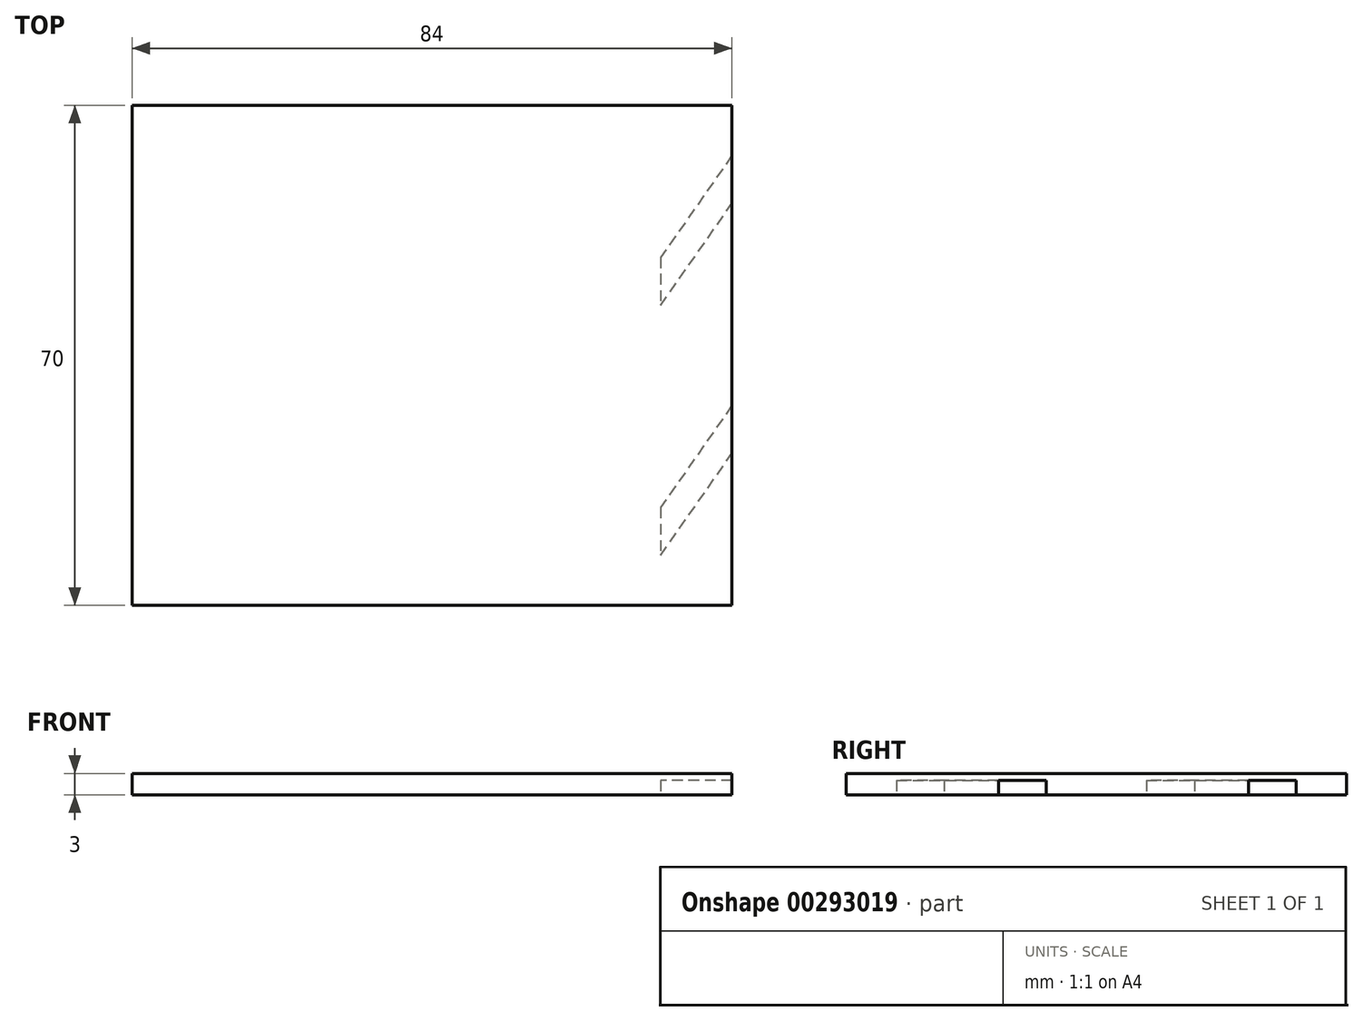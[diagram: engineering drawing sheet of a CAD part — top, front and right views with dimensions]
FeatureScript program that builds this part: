
annotation { "Feature Type Name" : "Feature", "Feature Type Description" : "" }
export const myFeature = defineFeature(function(context is Context, id is Id, definition is map)
    precondition{}
    {
        {
            var Q0;
            Q0=qCreatedBy(makeId("Front.planeOp"),FACE);
            var sketch = newSketch(context, id + "F0", { "sketchPlane" : qUnion([Q0])});
            skLineSegment(sketch, "E0.bottom", {"start": v(0, -23) * mm, "end": v(42, -23) * mm});
            skLineSegment(sketch, "E0.top", {"start": v(0, -20) * mm, "end": v(42, -20) * mm});
            skLineSegment(sketch, "E0.left", {"start": v(0, -23) * mm, "end": v(0, -20) * mm});
            skLineSegment(sketch, "E0.right", {"start": v(42, -23) * mm, "end": v(42, -20) * mm});
            skLineSegment(sketch, "E1", {"start": v(0, 0) * mm, "end": v(0, -20) * mm, "construction": true});
            skLineSegment(sketch, "E2", {"start": v(42, -21.5) * mm, "end": v(34, -21.5) * mm, "construction": true});
            skPoint(sketch, "E2.endSnap0", {"position": v(42, -21.5) * mm});
            skLineSegment(sketch, "E3", {"start": v(34, -21.5) * mm, "end": v(32, -21.5) * mm, "construction": true});
            skLineSegment(sketch, "E4", {"start": v(32, -21.5) * mm, "end": v(30, -21.5) * mm, "construction": true});
            skLineSegment(sketch, "E5", {"start": v(30, -21.5) * mm, "end": v(21, -21.5) * mm, "construction": true});
            skLineSegment(sketch, "E6", {"start": v(21, -21.5) * mm, "end": v(17, -21.5) * mm, "construction": true});
            skLineSegment(sketch, "E7", {"start": v(17, -21.5) * mm, "end": v(0, -21.5) * mm, "construction": true});
            skLineSegment(sketch, "E8", {"start": v(32, -21.5) * mm, "end": v(32, -23) * mm, "construction": true});
            skLineSegment(sketch, "E9", {"start": v(32, -23) * mm, "end": v(32, -21) * mm});
            skPoint(sketch, "E9.endSnap0", {"position": v(32, -22.25) * mm});
            skLineSegment(sketch, "E10", {"start": v(32, -21) * mm, "end": v(42, -21) * mm});
            skLineSegment(sketch, "E11", {"start": v(32, -22.25) * mm, "end": v(38, -22.25) * mm, "construction": true});
            skLineSegment(sketch, "E12", {"start": v(38, -22.25) * mm, "end": v(38, -23) * mm});
            skLineSegment(sketch, "E13", {"start": v(38, -23) * mm, "end": v(38, -21) * mm});
            skLineSegment(sketch, "E14.MirrorCS", {"start": v(-32, -23) * mm, "end": v(-32, -21) * mm});
            skLineSegment(sketch, "E15.MirrorCS", {"start": v(-32, -21.5) * mm, "end": v(-32, -23) * mm, "construction": true});
            skLineSegment(sketch, "E16.MirrorCS", {"start": v(-34, -21.5) * mm, "end": v(-32, -21.5) * mm, "construction": true});
            skLineSegment(sketch, "E17.MirrorCS", {"start": v(-32, -21.5) * mm, "end": v(-30, -21.5) * mm, "construction": true});
            skLineSegment(sketch, "E18.MirrorCS", {"start": v(-38, -23) * mm, "end": v(-38, -21) * mm});
            skLineSegment(sketch, "E19.MirrorCS", {"start": v(-38, -22.25) * mm, "end": v(-38, -23) * mm});
            skLineSegment(sketch, "E20.MirrorCS", {"start": v(-42, -23) * mm, "end": v(-42, -20) * mm});
            skLineSegment(sketch, "E21.MirrorCS", {"start": v(-42, -21.5) * mm, "end": v(-34, -21.5) * mm, "construction": true});
            skLineSegment(sketch, "E22.MirrorCS", {"start": v(-32, -21) * mm, "end": v(-42, -21) * mm});
            skLineSegment(sketch, "E23.MirrorCS", {"start": v(-32, -22.25) * mm, "end": v(-38, -22.25) * mm, "construction": true});
            skPoint(sketch, "E24.MirrorP", {"position": v(-42, -21.5) * mm});
            skLineSegment(sketch, "E25.MirrorCS", {"start": v(-30, -21.5) * mm, "end": v(-21, -21.5) * mm, "construction": true});
            skPoint(sketch, "E26.MirrorP", {"position": v(-32, -22.25) * mm});
            skLineSegment(sketch, "E27.MirrorCS", {"start": v(-21, -21.5) * mm, "end": v(-17, -21.5) * mm, "construction": true});
            skLineSegment(sketch, "E28.MirrorCS", {"start": v(-21, 40) * mm, "end": v(-17, 40) * mm});
            skLineSegment(sketch, "E29.MirrorCS", {"start": v(-30, 40) * mm, "end": v(-34, 40) * mm});
            skLineSegment(sketch, "E30.MirrorCS", {"start": v(0, -23) * mm, "end": v(-42, -23) * mm});
            skLineSegment(sketch, "E31.MirrorCS", {"start": v(-30, 40) * mm, "end": v(-30, -21.5) * mm});
            skLineSegment(sketch, "E32.MirrorCS", {"start": v(-17, 40) * mm, "end": v(-17, -21.5) * mm});
            skLineSegment(sketch, "E33.MirrorCS", {"start": v(-34, -21.5) * mm, "end": v(-34, 40) * mm});
            skLineSegment(sketch, "E34.MirrorCS", {"start": v(0, -20) * mm, "end": v(-42, -20) * mm});
            skLineSegment(sketch, "E35.MirrorCS", {"start": v(-17, -21.5) * mm, "end": v(0, -21.5) * mm, "construction": true});
            skLineSegment(sketch, "E36.MirrorCS", {"start": v(-21, -21.5) * mm, "end": v(-21, 40) * mm});
            skSolve(sketch);
        }
        {
            var Q0;
            {var subQ5=sQuery(id+"F0.wireOp",EDGE,"rBg3Q4IR-CGkZ-PO5m-HV7D-72pnYfLjL1so");Q0=makeQuery(id+"F0.imprint","IMPRINT",FACE,{"disambiguationData":[TD([[makeQuery(id+"F0.imprint","IMPRINT",EDGE,{"derivedFrom":subQ5}),1.0]])]});}
            var Q1;
            {var subQ5=sQuery(id+"F0.wireOp",EDGE,"dkqnGSy7-Vz6o-ykO8-f6sr-zODuD2kIRj3Q");Q1=makeQuery(id+"F0.imprint","IMPRINT",FACE,{"disambiguationData":[TD([[makeQuery(id+"F0.imprint","IMPRINT",EDGE,{"derivedFrom":subQ5}),-1.0]])]});}
            var Q2;
            {var subQ10=sQuery(id+"F0.wireOp",EDGE,"E9");Q2=makeQuery(id+"F0.imprint","IMPRINT",FACE,{"disambiguationData":[TD([[makeQuery(id+"F0.imprint","IMPRINT",EDGE,{"derivedFrom":subQ10}),1.0]])]});}
            var Q3;
            {var subQ1=sQuery(id+"F0.wireOp",EDGE,"E0.right");var subQ4=sQuery(id+"F0.wireOp",EDGE,"E0.top");var subQ5=makeQuery(id+"F0.imprint","INTERSECT",VERTEX,{"derivedFrom":[subQ4,subQ1]});Q3=makeQuery(id+"F0.imprint","IMPRINT",FACE,{"disambiguationData":[TD([[makeQuery(id+"F0.imprint","IMPRINT",EDGE,{"disambiguationData":[TD([[subQ5,1.0]])],"derivedFrom":subQ4}),-1.0]])]});}
            var Q4;
            {var subQ4=sQuery(id+"F0.wireOp",EDGE,"E9");Q4=makeQuery(id+"F0.imprint","IMPRINT",FACE,{"disambiguationData":[TD([[makeQuery(id+"F0.imprint","IMPRINT",EDGE,{"derivedFrom":subQ4}),-1.0]])]});}
            var Q5;
            {var subQ0=sQuery(id+"F0.wireOp",EDGE,"E13");var subQ3=makeQuery(id+"F0.imprint","IMPRINT",VERTEX,{"derivedFrom":subQ0});Q5=makeQuery(id+"F0.imprint","IMPRINT",FACE,{"disambiguationData":[TD([[makeQuery(id+"F0.imprint","IMPRINT",EDGE,{"disambiguationData":[TD([[subQ3,1.0]])],"derivedFrom":subQ0}),-1.0]])]});}
            var Q6;
            {var subQ6=sQuery(id+"F0.wireOp",EDGE,"E0.left");Q6=makeQuery(id+"F0.imprint","IMPRINT",FACE,{"disambiguationData":[TD([[makeQuery(id+"F0.imprint","IMPRINT",EDGE,{"derivedFrom":subQ6}),1.0]])]});}
            var Q7;
            {var subQ1=sQuery(id+"F0.wireOp",EDGE,"E22.MirrorCS");var subQ8=makeQuery(id+"F0.imprint","INTERSECT",VERTEX,{"derivedFrom":[sQuery(id+"F0.wireOp",EDGE,"E18.MirrorCS"),subQ1]});Q7=makeQuery(id+"F0.imprint","IMPRINT",FACE,{"disambiguationData":[TD([[makeQuery(id+"F0.imprint","IMPRINT",EDGE,{"disambiguationData":[TD([[subQ8,1.0]])],"derivedFrom":subQ1}),-1.0]])]});}
            var Q8;
            {var subQ1=sQuery(id+"F0.wireOp",EDGE,"E18.MirrorCS");var subQ5=makeQuery(id+"F0.imprint","IMPRINT",VERTEX,{"derivedFrom":subQ1});Q8=makeQuery(id+"F0.imprint","IMPRINT",FACE,{"disambiguationData":[TD([[makeQuery(id+"F0.imprint","IMPRINT",EDGE,{"disambiguationData":[TD([[subQ5,1.0]])],"derivedFrom":subQ1}),1.0]])]});}
            var Q9;
            {var subQ1=sQuery(id+"F0.wireOp",EDGE,"E14.MirrorCS");Q9=makeQuery(id+"F0.imprint","IMPRINT",FACE,{"disambiguationData":[TD([[makeQuery(id+"F0.imprint","IMPRINT",EDGE,{"derivedFrom":subQ1}),1.0]])]});}
            extrude(context, id + "F1", {"entities" : qUnion([Q0, Q1, Q2, Q3, Q4, Q5, Q6, Q7, Q8, Q9]), "depth" : 70 * mm});
        }
        {
            var Q0;
            Q0=makeQuery(id+"F1.opExtrude","SWEPT_FACE",FACE,{"disambiguationData":[OSD([sQuery(id+"F0.wireOp",EDGE,"E0.bottom"),sQuery(id+"F0.wireOp",EDGE,"E30.MirrorCS")])]});
            var sketch = newSketch(context, id + "F2", { "sketchPlane" : qUnion([Q0])});
            skLineSegment(sketch, "E37", {"start": v(42, 0) * mm, "end": v(-42, 0) * mm, "construction": true});
            skLineSegment(sketch, "E38", {"start": v(-42, 0) * mm, "end": v(-42, 70) * mm, "construction": true});
            skLineSegment(sketch, "E39", {"start": v(-42, 70) * mm, "end": v(42, 70) * mm, "construction": true});
            skLineSegment(sketch, "E40", {"start": v(0, 70) * mm, "end": v(0, 0) * mm});
            skLineSegment(sketch, "E41", {"start": v(42, 35) * mm, "end": v(42, 0) * mm, "construction": true});
            skLineSegment(sketch, "E42.MirrorCS", {"start": v(-42, 35) * mm, "end": v(42, 35) * mm});
            skLineSegment(sketch, "E43.MirrorCS", {"start": v(42, 35) * mm, "end": v(42, 70) * mm, "construction": true});
            skLineSegment(sketch, "E44", {"start": v(42, 70) * mm, "end": v(42, 0) * mm, "construction": true});
            skLineSegment(sketch, "E45", {"start": v(42, 70) * mm, "end": v(32, 70) * mm, "construction": true});
            skLineSegment(sketch, "E46", {"start": v(32, 70) * mm, "end": v(32, 35) * mm, "construction": true});
            skLineSegment(sketch, "E47", {"start": v(32, 35) * mm, "end": v(42, 35) * mm, "construction": true});
            skLineSegment(sketch, "E48", {"start": v(42, 42) * mm, "end": v(32, 56.28) * mm});
            skLineSegment(sketch, "E49", {"start": v(32, 56.28) * mm, "end": v(32, 63) * mm});
            skLineSegment(sketch, "E50", {"start": v(32, 63) * mm, "end": v(42, 48.72) * mm});
            skLineSegment(sketch, "E51", {"start": v(42, 48.72) * mm, "end": v(42, 42) * mm});
            skLineSegment(sketch, "E52.MirrorCS", {"start": v(-32, 63) * mm, "end": v(-42, 48.72) * mm});
            skLineSegment(sketch, "E53.MirrorCS", {"start": v(-42, 42) * mm, "end": v(-32, 56.28) * mm});
            skLineSegment(sketch, "E54.MirrorCS", {"start": v(-32, 70) * mm, "end": v(-32, 35) * mm, "construction": true});
            skLineSegment(sketch, "E55", {"start": v(-32, 63) * mm, "end": v(-32, 56.28) * mm});
            skLineSegment(sketch, "E56", {"start": v(-42, 48.72) * mm, "end": v(-42, 42) * mm});
            skLineSegment(sketch, "E57", {"start": v(-42, 0) * mm, "end": v(-42, 7) * mm, "construction": true});
            skLineSegment(sketch, "E58", {"start": v(42, 0) * mm, "end": v(42, 7) * mm, "construction": true});
            skLineSegment(sketch, "E59.MirrorCS", {"start": v(-32, 0) * mm, "end": v(-32, 35) * mm, "construction": true});
            skLineSegment(sketch, "E60", {"start": v(32, 35) * mm, "end": v(32, 0) * mm, "construction": true});
            skLineSegment(sketch, "E61", {"start": v(32, 35) * mm, "end": v(32, 28) * mm, "construction": true});
            skLineSegment(sketch, "E62", {"start": v(-32, 35) * mm, "end": v(-32, 28) * mm, "construction": true});
            skLineSegment(sketch, "E63", {"start": v(-42, 7) * mm, "end": v(-32, 21.28) * mm});
            skLineSegment(sketch, "E64", {"start": v(42, 7) * mm, "end": v(32, 21.28) * mm});
            skLineSegment(sketch, "E65", {"start": v(-32, 28) * mm, "end": v(-42, 13.72) * mm});
            skLineSegment(sketch, "E66", {"start": v(32, 28) * mm, "end": v(42, 13.72) * mm});
            skLineSegment(sketch, "E67", {"start": v(42, 13.72) * mm, "end": v(42, 7) * mm});
            skLineSegment(sketch, "E68", {"start": v(32, 21.28) * mm, "end": v(32, 28) * mm});
            skLineSegment(sketch, "E69", {"start": v(-42, 13.72) * mm, "end": v(-42, 7) * mm});
            skLineSegment(sketch, "E70", {"start": v(-32, 28) * mm, "end": v(-32, 21.28) * mm});
            skLineSegment(sketch, "E71", {"start": v(42, 7) * mm, "end": v(42, 13.72) * mm});
            skLineSegment(sketch, "E72", {"start": v(-42, 7) * mm, "end": v(-42, 13.72) * mm});
            skLineSegment(sketch, "E73", {"start": v(-42, 42) * mm, "end": v(-42, 48.72) * mm});
            skSolve(sketch);
        }
        {
            var Q0;
            Q0=makeQuery(id+"F2.imprint","IMPRINT",FACE,{"disambiguationData":[TD([[makeQuery(id+"F2.imprint","IMPRINT",EDGE,{"derivedFrom":sQuery(id+"F2.wireOp",EDGE,"E48")}),-1.0]])]});
            var Q1;
            Q1=makeQuery(id+"F2.imprint","IMPRINT",FACE,{"disambiguationData":[TD([[makeQuery(id+"F2.imprint","IMPRINT",EDGE,{"derivedFrom":sQuery(id+"F2.wireOp",EDGE,"E64")}),-1.0]])]});
            extrude(context, id + "F3", {"entities" : qUnion([Q0, Q1]), "operationType" : NewBodyOperationType.REMOVE, "oppositeDirection" : true, "depth" : 2 * mm});
        }
    });
